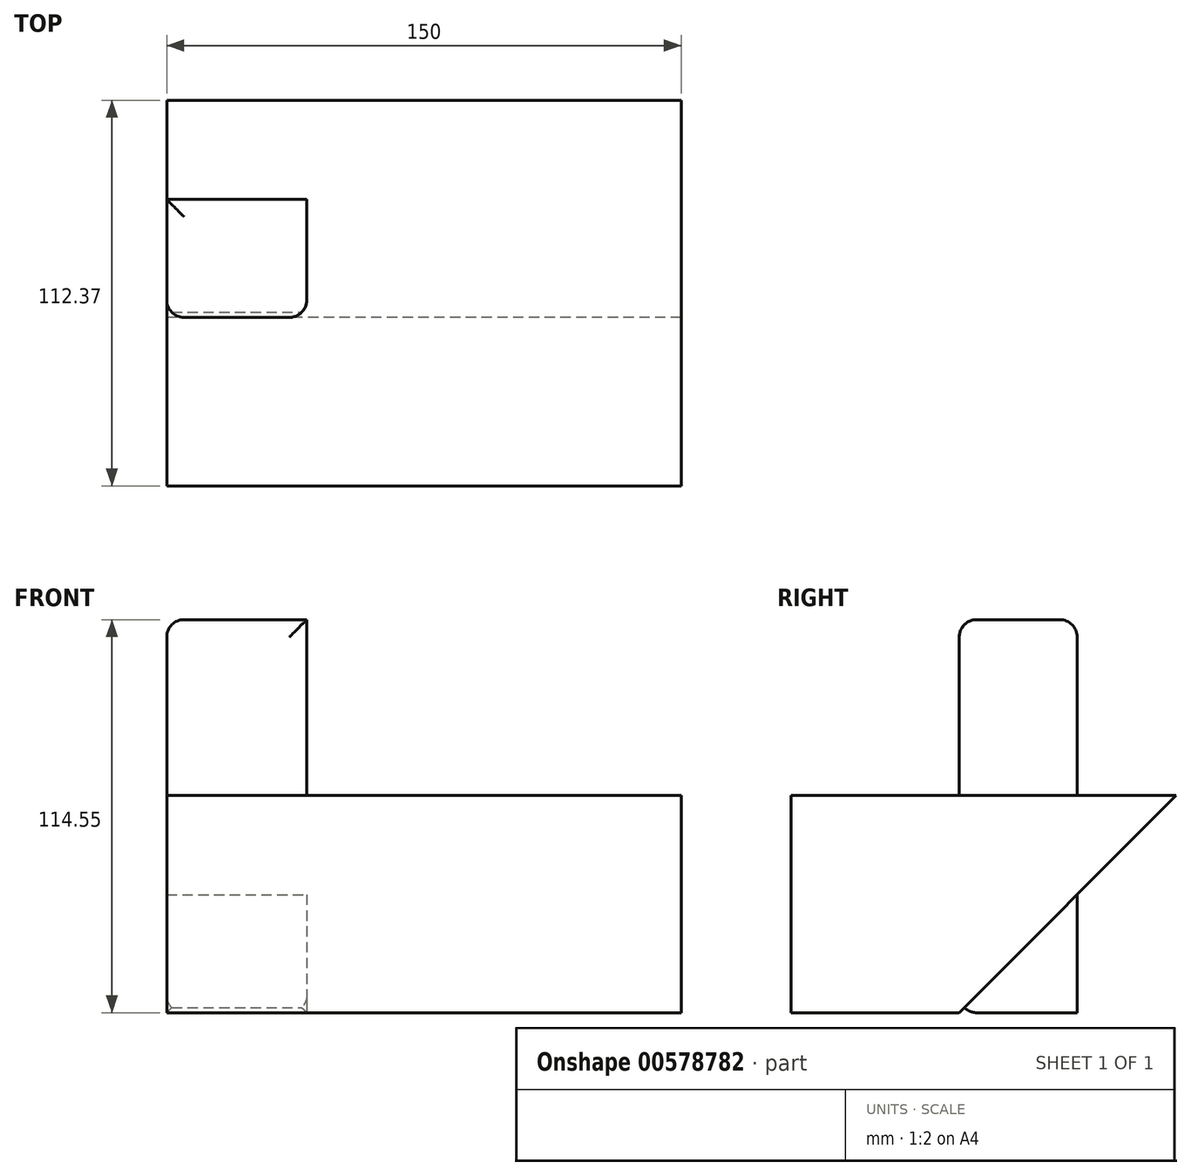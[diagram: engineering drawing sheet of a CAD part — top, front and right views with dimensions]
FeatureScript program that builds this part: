
annotation { "Feature Type Name" : "Feature", "Feature Type Description" : "" }
export const myFeature = defineFeature(function(context is Context, id is Id, definition is map)
    precondition{}
    {
        {
            var Q0;
            Q0=qCreatedBy(makeId("Top.planeOp"),FACE);
            var sketch = newSketch(context, id + "F0", { "sketchPlane" : qUnion([Q0])});
            skLineSegment(sketch, "E0", {"start": v(0, 0) * mm, "end": v(40.85, 0) * mm});
            skLineSegment(sketch, "E1", {"start": v(40.85, 0) * mm, "end": v(40.85, 34.37) * mm});
            skLineSegment(sketch, "E2", {"start": v(40.85, 34.37) * mm, "end": v(0, 34.37) * mm});
            skLineSegment(sketch, "E3", {"start": v(0, 34.37) * mm, "end": v(0, 0) * mm});
            skSolve(sketch);
        }
        {
            var Q0;
            Q0=makeQuery(id+"F0.imprint","IMPRINT",FACE,{"disambiguationData":[TD([[makeQuery(id+"F0.imprint","IMPRINT",EDGE,{"derivedFrom":sQuery(id+"F0.wireOp",EDGE,"E0")}),1.0]])]});
            extrude(context, id + "F1", {"entities" : qUnion([Q0]), "depth" : 114.55 * mm, "offsetDistance" : 25.4 * mm});
        }
        {
            var Q0;
            Q0=makeQuery(id+"F1.opExtrude","CAP_EDGE",EDGE,{"disambiguationData":[OSD([sQuery(id+"F0.wireOp",EDGE,"E0")])],"isStart":false});
            var Q1;
            Q1=makeQuery(id+"F1.opExtrude","CAP_EDGE",EDGE,{"disambiguationData":[OSD([sQuery(id+"F0.wireOp",EDGE,"E2")])],"isStart":false});
            var Q2;
            Q2=makeQuery(id+"F1.opExtrude","SWEPT_EDGE",EDGE,{"disambiguationData":[OSD([sQuery(id+"F0.wireOp",EDGE,"E0"),sQuery(id+"F0.wireOp",EDGE,"E3")])]});
            var Q3;
            Q3=makeQuery(id+"F1.opExtrude","CAP_EDGE",EDGE,{"disambiguationData":[OSD([sQuery(id+"F0.wireOp",EDGE,"E3")])],"isStart":false});
            var Q4;
            Q4=makeQuery(id+"F1.opExtrude","SWEPT_EDGE",EDGE,{"disambiguationData":[OSD([sQuery(id+"F0.wireOp",EDGE,"E0"),sQuery(id+"F0.wireOp",EDGE,"E1")])]});
            var Q5;
            Q5=makeQuery(id+"F1.opExtrude","CAP_EDGE",EDGE,{"disambiguationData":[OSD([sQuery(id+"F0.wireOp",EDGE,"E0")])],"isStart":true});
            fillet(context, id + "F2", {"entities" : qUnion([Q0, Q1, Q2, Q3, Q4, Q5]), "radius" : 5.08 * mm, "tangentPropagation" : true, "allowEdgeOverflow" : false});
        }
        {
            var Q0;
            Q0=qCreatedBy(makeId("Right.planeOp"),FACE);
            var sketch = newSketch(context, id + "F3", { "sketchPlane" : qUnion([Q0])});
            skLineSegment(sketch, "E4", {"start": v(0, 0) * mm, "end": v(-49.09, 0) * mm});
            skLineSegment(sketch, "E5", {"start": v(-49.09, 0) * mm, "end": v(-49.09, 63.3) * mm});
            skLineSegment(sketch, "E6", {"start": v(-49.09, 63.3) * mm, "end": v(63.28, 63.3) * mm});
            skLineSegment(sketch, "E7", {"start": v(63.28, 63.3) * mm, "end": v(0, 0) * mm});
            skSolve(sketch);
        }
        {
            var Q0;
            Q0=makeQuery(id+"F3.imprint","IMPRINT",FACE,{"disambiguationData":[TD([[makeQuery(id+"F3.imprint","IMPRINT",EDGE,{"derivedFrom":sQuery(id+"F3.wireOp",EDGE,"E4")}),-1.0]])]});
            extrude(context, id + "F4", {"entities" : qUnion([Q0]), "operationType" : NewBodyOperationType.ADD, "depth" : 150 * mm, "offsetDistance" : 25 * mm});
        }
    });
